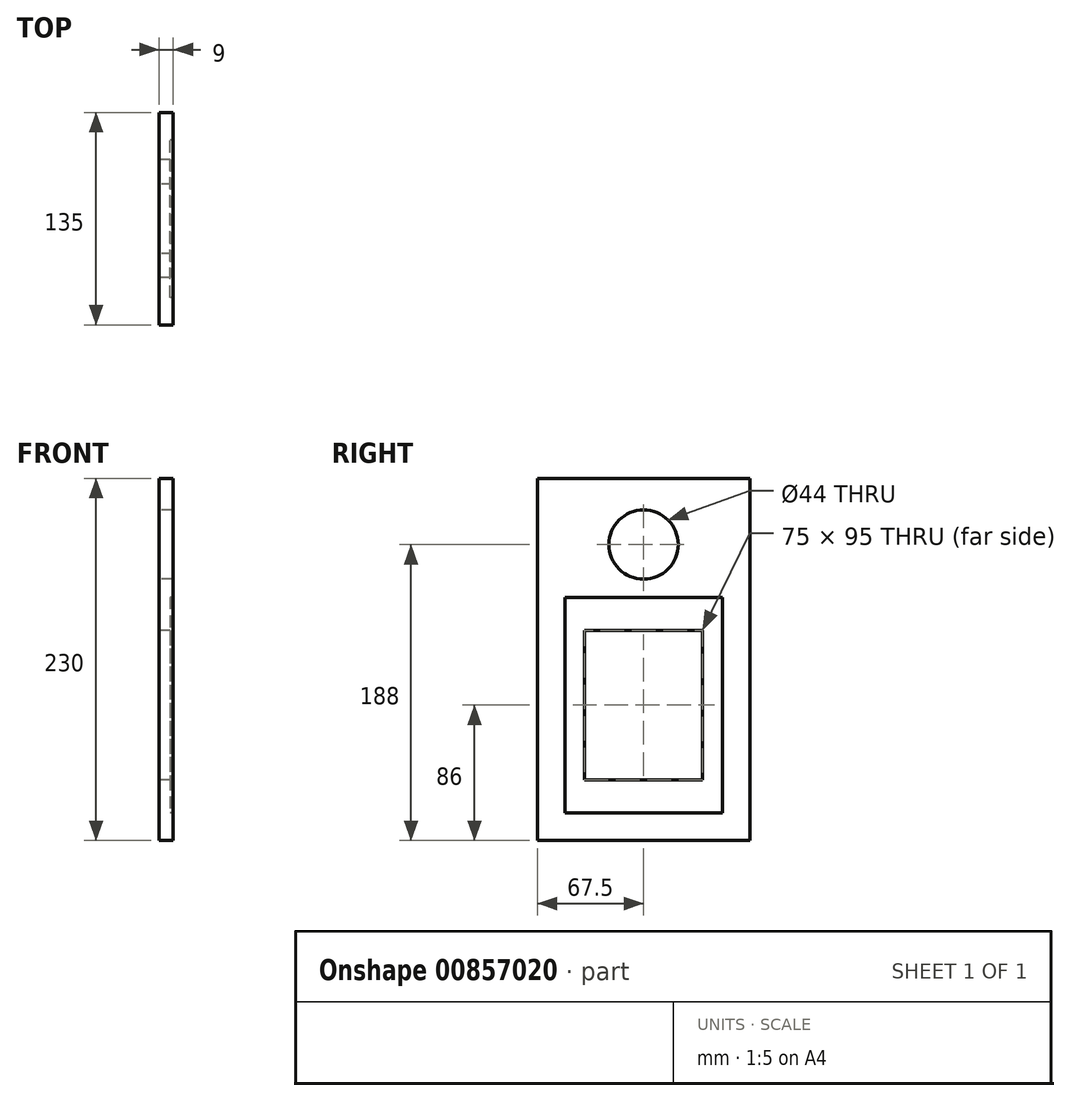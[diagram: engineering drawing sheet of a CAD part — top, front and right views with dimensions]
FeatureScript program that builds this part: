
annotation { "Feature Type Name" : "Feature", "Feature Type Description" : "" }
export const myFeature = defineFeature(function(context is Context, id is Id, definition is map)
    precondition{}
    {
        {
            var Q0;
            Q0=qCreatedBy(makeId("Right.planeOp"),FACE);
            var sketch = newSketch(context, id + "F0", { "sketchPlane" : qUnion([Q0])});
            skLineSegment(sketch, "E0.bottom", {"start": v(-67.5, 115) * mm, "end": v(67.5, 115) * mm});
            skLineSegment(sketch, "E0.top", {"start": v(-67.5, -115) * mm, "end": v(67.5, -115) * mm});
            skLineSegment(sketch, "E0.left", {"start": v(-67.5, 115) * mm, "end": v(-67.5, -115) * mm});
            skLineSegment(sketch, "E0.right", {"start": v(67.5, 115) * mm, "end": v(67.5, -115) * mm});
            skPoint(sketch, "E0.middle", {"position": v(0, 0) * mm});
            skLineSegment(sketch, "E1", {"start": v(0, 115) * mm, "end": v(0, -115) * mm});
            skLineSegment(sketch, "E2.left", {"start": v(-50, 30.45) * mm, "end": v(-50, -97.5) * mm});
            skLineSegment(sketch, "E2.right", {"start": v(50, 30.45) * mm, "end": v(50, -97.5) * mm});
            skPoint(sketch, "E2.middle", {"position": v(0, -37.9) * mm});
            skPoint(sketch, "E3", {"position": v(0, -97.5) * mm});
            skPoint(sketch, "E4", {"position": v(0, -29) * mm});
            skLineSegment(sketch, "E5.bottom", {"start": v(-50, 39.5) * mm, "end": v(50, 39.5) * mm});
            skLineSegment(sketch, "E5.left", {"start": v(-50, 39.5) * mm, "end": v(-50, -97.5) * mm});
            skLineSegment(sketch, "E5.right", {"start": v(50, 39.5) * mm, "end": v(50, -97.5) * mm});
            skLineSegment(sketch, "E6", {"start": v(-50, -97.5) * mm, "end": v(50, -97.5) * mm});
            skLineSegment(sketch, "E7.bottom", {"start": v(37.5, 18.5) * mm, "end": v(-37.5, 18.5) * mm});
            skLineSegment(sketch, "E7.top", {"start": v(37.5, -76.5) * mm, "end": v(-37.5, -76.5) * mm});
            skLineSegment(sketch, "E7.left", {"start": v(37.5, 18.5) * mm, "end": v(37.5, -76.5) * mm});
            skLineSegment(sketch, "E7.right", {"start": v(-37.5, 18.5) * mm, "end": v(-37.5, -76.5) * mm});
            skCircle(sketch, "E8", {"center": v(0, 73) * mm, "radius": 22 * mm});
            skCircle(sketch, "E9", {"center": v(0, 73) * mm, "radius": 16.5 * mm});
            skSolve(sketch);
        }
        {
            var Q0;
            {var subQ12=sQuery(id+"F0.wireOp",EDGE,"E0.left");Q0=makeQuery(id+"F0.imprint","IMPRINT",FACE,{"disambiguationData":[TD([[makeQuery(id+"F0.imprint","IMPRINT",EDGE,{"derivedFrom":subQ12}),1.0]])]});}
            var Q1;
            {var subQ11=sQuery(id+"F0.wireOp",EDGE,"E0.right");Q1=makeQuery(id+"F0.imprint","IMPRINT",FACE,{"disambiguationData":[TD([[makeQuery(id+"F0.imprint","IMPRINT",EDGE,{"derivedFrom":subQ11}),-1.0]])]});}
            extrude(context, id + "F1", {"entities" : qUnion([Q0, Q1]), "depth" : 9 * mm, "offsetDistance" : 25 * mm});
        }
        {
            var Q0;
            {var subQ0=sQuery(id+"F0.wireOp",EDGE,"E8");var subQ1=sQuery(id+"F0.wireOp",EDGE,"E1");var subQ2=makeQuery(id+"F0.imprint","INTERSECT",VERTEX,{"disambiguationData":[OD(0.0)],"derivedFrom":[subQ1,subQ0]});Q0=makeQuery(id+"F0.imprint","IMPRINT",FACE,{"disambiguationData":[TD([[makeQuery(id+"F0.imprint","IMPRINT",EDGE,{"disambiguationData":[TD([[subQ2,-1.0]])],"derivedFrom":subQ1}),-1.0]])]});}
            var Q1;
            {var subQ0=sQuery(id+"F0.wireOp",EDGE,"E8");var subQ1=sQuery(id+"F0.wireOp",EDGE,"E1");var subQ2=makeQuery(id+"F0.imprint","INTERSECT",VERTEX,{"disambiguationData":[OD(0.0)],"derivedFrom":[subQ1,subQ0]});Q1=makeQuery(id+"F0.imprint","IMPRINT",FACE,{"disambiguationData":[TD([[makeQuery(id+"F0.imprint","IMPRINT",EDGE,{"disambiguationData":[TD([[subQ2,-1.0]])],"derivedFrom":subQ1}),1.0]])]});}
            extrude(context, id + "F2", {"entities" : qUnion([Q0, Q1]), "operationType" : NewBodyOperationType.ADD, "depth" : 6 * mm, "offsetDistance" : 25 * mm});
        }
        {
            var Q0;
            {var subQ4=sQuery(id+"F0.wireOp",EDGE,"E7.right");Q0=makeQuery(id+"F0.imprint","IMPRINT",FACE,{"disambiguationData":[TD([[makeQuery(id+"F0.imprint","IMPRINT",EDGE,{"derivedFrom":subQ4}),-1.0]])]});}
            var Q1;
            {var subQ10=sQuery(id+"F0.wireOp",EDGE,"E7.left");Q1=makeQuery(id+"F0.imprint","IMPRINT",FACE,{"disambiguationData":[TD([[makeQuery(id+"F0.imprint","IMPRINT",EDGE,{"derivedFrom":subQ10}),1.0]])]});}
            extrude(context, id + "F3", {"entities" : qUnion([Q0, Q1]), "operationType" : NewBodyOperationType.ADD, "depth" : 7 * mm, "offsetDistance" : 25 * mm});
        }
    });
